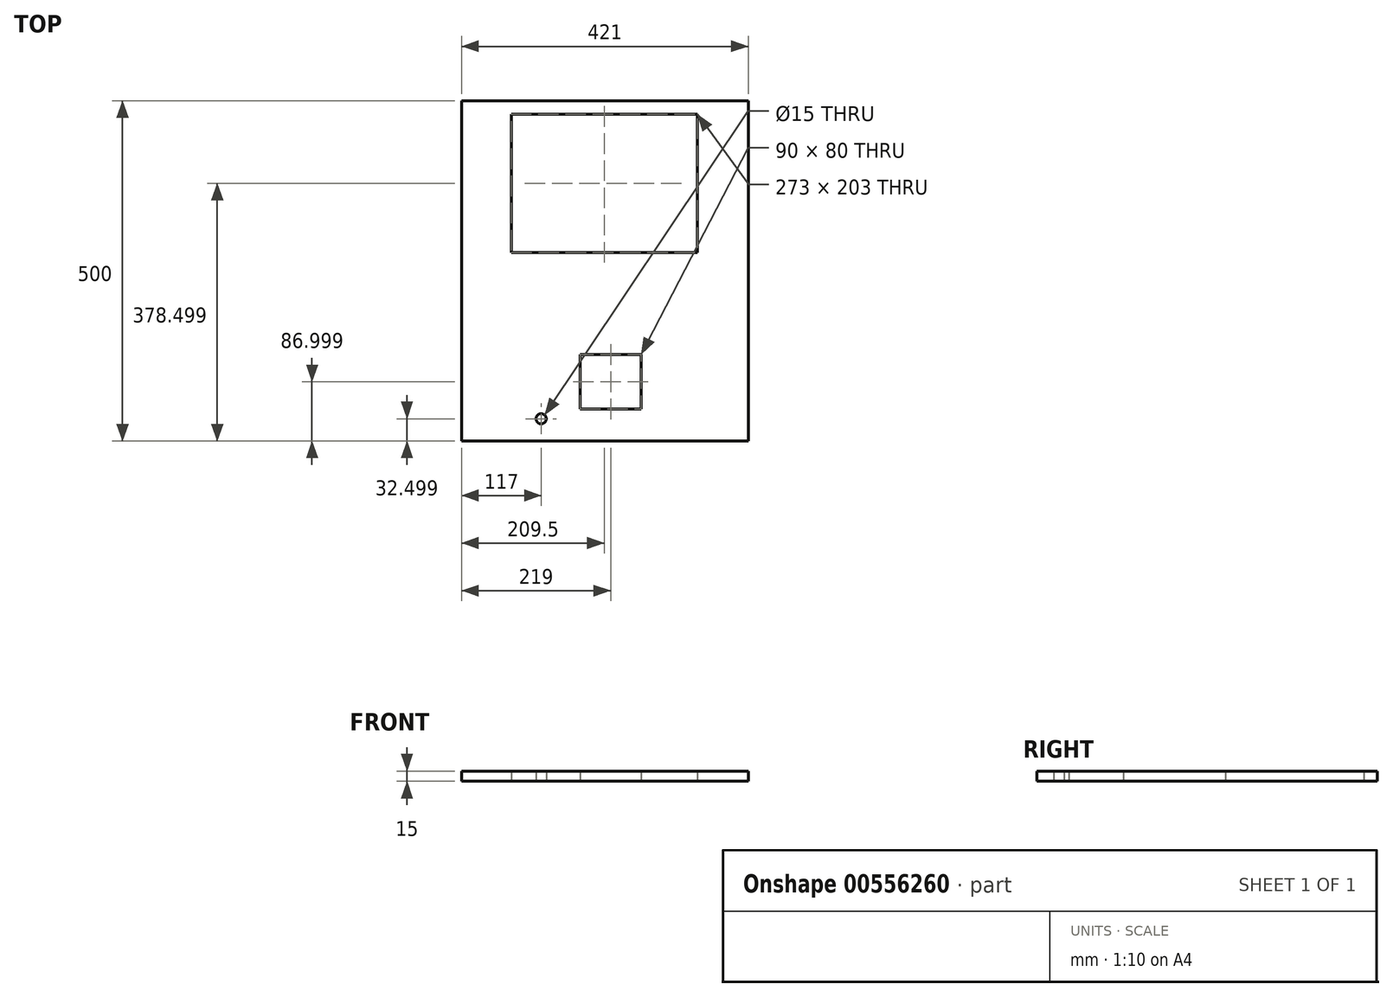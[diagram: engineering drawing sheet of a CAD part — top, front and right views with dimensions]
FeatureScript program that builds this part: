
annotation { "Feature Type Name" : "Feature", "Feature Type Description" : "" }
export const myFeature = defineFeature(function(context is Context, id is Id, definition is map)
    precondition{}
    {
        {
            var Q0;
            Q0=qCreatedBy(makeId("Top.planeOp"),FACE);
            var sketch = newSketch(context, id + "F0", { "sketchPlane" : qUnion([Q0])});
            skLineSegment(sketch, "E0.bottom", {"start": v(-174, 203.78) * mm, "end": v(247, 203.78) * mm});
            skLineSegment(sketch, "E0.top", {"start": v(-174, -296.22) * mm, "end": v(247, -296.22) * mm});
            skLineSegment(sketch, "E0.left", {"start": v(-174, 203.78) * mm, "end": v(-174, -296.22) * mm});
            skLineSegment(sketch, "E0.right", {"start": v(247, 203.78) * mm, "end": v(247, -296.22) * mm});
            skLineSegment(sketch, "E1.bottom", {"start": v(-101, 183.78) * mm, "end": v(172, 183.78) * mm});
            skLineSegment(sketch, "E1.top", {"start": v(-101, -19.22) * mm, "end": v(172, -19.22) * mm});
            skLineSegment(sketch, "E1.left", {"start": v(-101, 183.78) * mm, "end": v(-101, -19.22) * mm});
            skLineSegment(sketch, "E1.right", {"start": v(172, 183.78) * mm, "end": v(172, -19.22) * mm});
            skLineSegment(sketch, "E2.bottom", {"start": v(0, -169.22) * mm, "end": v(90, -169.22) * mm});
            skLineSegment(sketch, "E2.top", {"start": v(0, -249.22) * mm, "end": v(90, -249.22) * mm});
            skLineSegment(sketch, "E2.left", {"start": v(0, -169.22) * mm, "end": v(0, -249.22) * mm});
            skLineSegment(sketch, "E2.right", {"start": v(90, -169.22) * mm, "end": v(90, -249.22) * mm});
            skCircle(sketch, "E3", {"center": v(-57, -263.72) * mm, "radius": 7.5 * mm});
            skPoint(sketch, "E4.startSnap0", {"position": v(35.5, -19.22) * mm});
            skLineSegment(sketch, "E5", {"start": v(150, -56.22) * mm, "end": v(150, -276.22) * mm, "construction": true});
            skLineSegment(sketch, "E6.MirrorCS", {"start": v(-80, -56.22) * mm, "end": v(-80, -276.22) * mm, "construction": true});
            skLineSegment(sketch, "E7", {"start": v(-80, -56.22) * mm, "end": v(150, -56.22) * mm, "construction": true});
            skLineSegment(sketch, "E8", {"start": v(150, -276.22) * mm, "end": v(-80, -276.22) * mm, "construction": true});
            skSolve(sketch);
        }
        {
            var Q0;
            Q0=makeQuery(id+"F0.imprint","IMPRINT",FACE,{"disambiguationData":[TD([[makeQuery(id+"F0.imprint","IMPRINT",EDGE,{"derivedFrom":sQuery(id+"F0.wireOp",EDGE,"E0.bottom")}),-1.0]])]});
            extrude(context, id + "F1", {"entities" : qUnion([Q0]), "depth" : 15 * mm, "offsetDistance" : 25 * mm});
        }
    });
